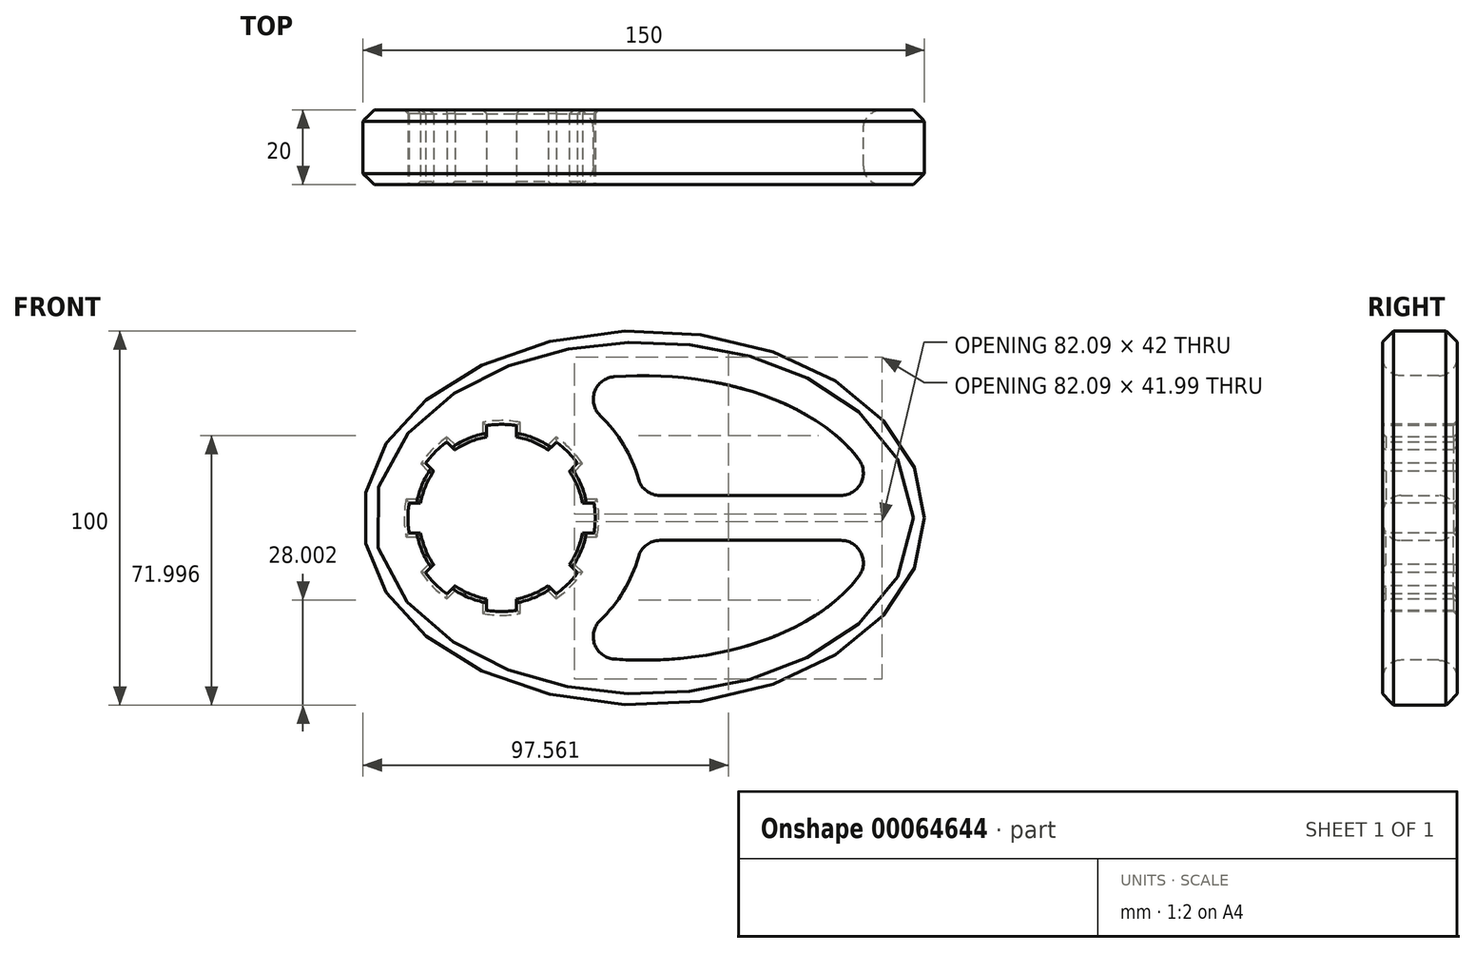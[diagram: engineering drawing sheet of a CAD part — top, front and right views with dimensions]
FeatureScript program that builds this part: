
annotation { "Feature Type Name" : "Feature", "Feature Type Description" : "" }
export const myFeature = defineFeature(function(context is Context, id is Id, definition is map)
    precondition{}
    {
        {
            var Q0;
            Q0=qCreatedBy(makeId("Front.planeOp"),FACE);
            var sketch = newSketch(context, id + "F0", { "sketchPlane" : qUnion([Q0])});
            skEllipse(sketch, "E0", {"center": v(0, 0) * mm, "majorRadius": 75 * mm, "minorRadius": 50 * mm, "majorAxis": v(1, 0)});
            skEllipticalArc(sketch, "E1", {});
            skLineSegment(sketch, "E2", {"start": v(0, 0) * mm, "end": v(-38, 0) * mm});
            skArc(sketch, "E3", {"start": v(-11.66, 27.39) * mm, "mid": v(-5.42, 19.56) * mm, "end": v(-1.44, 10.36) * mm});
            skArc(sketch, "E4", {"start": v(-7.96, 37.7) * mm, "mid": v(-13.15, 33.74) * mm, "end": v(-11.66, 27.39) * mm});
            skArc(sketch, "E5", {"start": v(-1.44, 10.36) * mm, "mid": v(0.71, 7.21) * mm, "end": v(4.33, 6) * mm});
            skArc(sketch, "E6", {"start": v(52.65, 6) * mm, "mid": v(58, 9.3) * mm, "end": v(57.46, 15.59) * mm});
            skLineSegment(sketch, "E7", {"start": v(4.33, 6) * mm, "end": v(52.65, 6) * mm});
            skLineSegment(sketch, "E8.MirrorCS", {"start": v(4.33, -6) * mm, "end": v(52.65, -6) * mm});
            skArc(sketch, "E9.MirrorCS", {"start": v(-1.44, -10.36) * mm, "mid": v(0.71, -7.21) * mm, "end": v(4.33, -6) * mm});
            skArc(sketch, "E10.MirrorCS", {"start": v(-11.66, -27.39) * mm, "mid": v(-5.42, -19.56) * mm, "end": v(-1.44, -10.36) * mm});
            skArc(sketch, "E11.MirrorCS", {"start": v(-7.96, -37.7) * mm, "mid": v(-13.15, -33.74) * mm, "end": v(-11.66, -27.39) * mm});
            skArc(sketch, "E12.MirrorCS", {"start": v(52.65, -6) * mm, "mid": v(58, -9.3) * mm, "end": v(57.46, -15.59) * mm});
            skEllipticalArc(sketch, "E13.trimOffspring", {});
            skCircle(sketch, "E14", {"center": v(-38, 0) * mm, "radius": 22 * mm});
            skPoint(sketch, "E15", {"position": v(75, 0) * mm});
            const initialGuessF0  = {"E1": [0, 0, 1, 0, 0.063, 0.038, 4.5857151122401865, 5.860542602533357], "E1": [0, 0, 1, 0, 0.063, 0.038, 4.5857151122401865, 5.860542602533357], "E13.trimOffspring": [0, 0, 1, 0, 0.063, 0.038, 0.42264270464622916, 1.6974701949393995], "E13.trimOffspring": [0, 0, 1, 0, 0.063, 0.038, 0.42264270464622916, 1.6974701949393995]};
            skSetInitialGuess(sketch, initialGuessF0);
            skSolve(sketch);
        }
        {
            var Q0;
            Q0=makeQuery(id+"F0.imprint","IMPRINT",FACE,{"disambiguationData":[TD([[makeQuery(id+"F0.imprint","IMPRINT",EDGE,{"derivedFrom":sQuery(id+"F0.wireOp",EDGE,"E0")}),1.0]])]});
            extrude(context, id + "F1", {"entities" : qUnion([Q0]), "flatOperationType" : FlatOperationType.REMOVE, "offsetDistance" : 25 * mm, "depth" : 20 * mm, "domain" : OperationDomain.MODEL});
        }
        {
            var Q0;
            Q0=makeQuery(id+"F1.opExtrude","CAP_FACE",FACE,{"disambiguationData":[OSD([sQuery(id+"F0.wireOp",EDGE,"E0"),sQuery(id+"F0.wireOp",EDGE,"E3"),sQuery(id+"F0.wireOp",EDGE,"E4"),sQuery(id+"F0.wireOp",EDGE,"E5"),sQuery(id+"F0.wireOp",EDGE,"E6"),sQuery(id+"F0.wireOp",EDGE,"E7"),sQuery(id+"F0.wireOp",EDGE,"E8.MirrorCS"),sQuery(id+"F0.wireOp",EDGE,"E9.MirrorCS"),sQuery(id+"F0.wireOp",EDGE,"E10.MirrorCS"),sQuery(id+"F0.wireOp",EDGE,"E11.MirrorCS"),sQuery(id+"F0.wireOp",EDGE,"E1"),sQuery(id+"F0.wireOp",EDGE,"E12.MirrorCS"),sQuery(id+"F0.wireOp",EDGE,"E13.trimOffspring"),sQuery(id+"F0.wireOp",EDGE,"E14")])],"isStart":false});
            var sketch = newSketch(context, id + "F2", { "sketchPlane" : qUnion([Q0])});
            skCircle(sketch, "E16", {"center": v(-38, 0) * mm, "radius": 25 * mm});
            skLineSegment(sketch, "E17", {"start": v(-13.32, 4) * mm, "end": v(-16.37, 4) * mm});
            skLineSegment(sketch, "E18", {"start": v(-13.32, -4) * mm, "end": v(-16.37, -4) * mm});
            skSolve(sketch);
        }
        {
            var Q0;
            {var subQ0=sQuery(id+"F2.wireOp",EDGE,"E17");Q0=makeQuery(id+"F2.imprint","IMPRINT",FACE,{"disambiguationData":[TD([[makeQuery(id+"F2.imprint","IMPRINT",EDGE,{"derivedFrom":subQ0}),1.0]])]});}
            extrude(context, id + "F3", {"entities" : qUnion([Q0]), "operationType" : NewBodyOperationType.REMOVE, "endBound" : BoundingType.THROUGH_ALL, "oppositeDirection" : true, "depth" : 25 * mm});
        }
        {
            var Q0;
            Q0=makeQuery(id+"F3.boolean.opBoolean","COPY",FACE,{"derivedFrom":makeQuery(id+"F3.opExtrude","SWEPT_FACE",FACE,{"disambiguationData":[OSD([sQuery(id+"F2.wireOp",EDGE,"E16")])]})});
            var Q1;
            Q1=makeQuery(id+"F3.boolean.opBoolean","COPY",FACE,{"derivedFrom":makeQuery(id+"F3.opExtrude","SWEPT_FACE",FACE,{"disambiguationData":[OSD([sQuery(id+"F2.wireOp",EDGE,"E18")])]})});
            var Q2;
            Q2=makeQuery(id+"F3.boolean.opBoolean","COPY",FACE,{"derivedFrom":makeQuery(id+"F3.opExtrude","SWEPT_FACE",FACE,{"disambiguationData":[OSD([sQuery(id+"F2.wireOp",EDGE,"E17")])]})});
            var Q3;
            Q3=makeQuery(id+"F1.opExtrude","SWEPT_FACE",FACE,{"disambiguationData":[OSD([sQuery(id+"F0.wireOp",EDGE,"E14")])]});
            circularPattern(context, id + "F4", {"operationType" : NewBodyOperationType.REMOVE, "faces" : qUnion([Q0, Q1, Q2]), "axis" : qUnion([Q3]), "angle" : 360 * degree, "instanceCount" : 8, "equalSpace" : true, "patternType" : PatternType.FACE});
        }
        {
            var Q0;
            Q0=makeQuery(id+"F1.opExtrude","CAP_EDGE",EDGE,{"disambiguationData":[OSD([sQuery(id+"F0.wireOp",EDGE,"E0")])],"isStart":false});
            var Q1;
            Q1=makeQuery(id+"F1.opExtrude","CAP_EDGE",EDGE,{"disambiguationData":[OSD([sQuery(id+"F0.wireOp",EDGE,"E0")])],"isStart":true});
            chamfer(context, id + "F5", {"entities" : qUnion([Q0, Q1]), "width" : 3 * mm, "tangentPropagation" : true});
        }
        {
            var Q0;
            Q0=makeQuery(id+"F1.opExtrude","CAP_EDGE",EDGE,{"disambiguationData":[OSD([sQuery(id+"F0.wireOp",EDGE,"E3")])],"isStart":false});
            var Q1;
            Q1=makeQuery(id+"F1.opExtrude","CAP_EDGE",EDGE,{"disambiguationData":[OSD([sQuery(id+"F0.wireOp",EDGE,"E10.MirrorCS")])],"isStart":false});
            var Q2;
            Q2=makeQuery(id+"F1.opExtrude","CAP_EDGE",EDGE,{"disambiguationData":[OSD([sQuery(id+"F0.wireOp",EDGE,"E8.MirrorCS")])],"isStart":true});
            var Q3;
            Q3=makeQuery(id+"F1.opExtrude","CAP_EDGE",EDGE,{"disambiguationData":[OSD([sQuery(id+"F0.wireOp",EDGE,"E7")])],"isStart":true});
            fillet(context, id + "F6", {"entities" : qUnion([Q0, Q1, Q2, Q3]), "radius" : 5 * mm, "tangentPropagation" : true, "allowEdgeOverflow" : false});
        }
        {
            var Q0;
            Q0=makeQuery(id+"F4.opPattern","COPY",EDGE,{"derivedFrom":makeQuery(id+"F3.boolean.opBoolean","COPY",EDGE,{"derivedFrom":makeQuery(id+"F3.opExtrude","CAP_EDGE",EDGE,{"disambiguationData":[OSD([sQuery(id+"F2.wireOp",EDGE,"E16")])],"isStart":true})}),"instanceName":"4"});
            var Q1;
            Q1=makeQuery(id+"F4.opPattern","COPY",EDGE,{"derivedFrom":makeQuery(id+"F3.boolean.opBoolean","COPY",EDGE,{"derivedFrom":makeQuery(id+"F3.opExtrude","CAP_EDGE",EDGE,{"disambiguationData":[OSD([sQuery(id+"F2.wireOp",EDGE,"E17")])],"isStart":true})}),"instanceName":"4"});
            var Q2;
            Q2=makeQuery(id+"F4.opPattern","SPLIT",EDGE,{"disambiguationData":[OD(5.0)],"derivedFrom":makeQuery(id+"F1.opExtrude","CAP_EDGE",EDGE,{"disambiguationData":[OSD([sQuery(id+"F0.wireOp",EDGE,"E14")])],"isStart":false})});
            var Q3;
            Q3=makeQuery(id+"F4.opPattern","COPY",EDGE,{"derivedFrom":makeQuery(id+"F3.boolean.opBoolean","COPY",EDGE,{"derivedFrom":makeQuery(id+"F3.opExtrude","CAP_EDGE",EDGE,{"disambiguationData":[OSD([sQuery(id+"F2.wireOp",EDGE,"E18")])],"isStart":true})}),"instanceName":"5"});
            var Q4;
            Q4=makeQuery(id+"F4.opPattern","COPY",EDGE,{"derivedFrom":makeQuery(id+"F3.boolean.opBoolean","COPY",EDGE,{"derivedFrom":makeQuery(id+"F3.opExtrude","CAP_EDGE",EDGE,{"disambiguationData":[OSD([sQuery(id+"F2.wireOp",EDGE,"E16")])],"isStart":true})}),"instanceName":"5"});
            var Q5;
            Q5=makeQuery(id+"F4.opPattern","COPY",EDGE,{"derivedFrom":makeQuery(id+"F3.boolean.opBoolean","COPY",EDGE,{"derivedFrom":makeQuery(id+"F3.opExtrude","CAP_EDGE",EDGE,{"disambiguationData":[OSD([sQuery(id+"F2.wireOp",EDGE,"E17")])],"isStart":true})}),"instanceName":"5"});
            var Q6;
            Q6=makeQuery(id+"F4.opPattern","SPLIT",EDGE,{"disambiguationData":[OD(6.0)],"derivedFrom":makeQuery(id+"F1.opExtrude","CAP_EDGE",EDGE,{"disambiguationData":[OSD([sQuery(id+"F0.wireOp",EDGE,"E14")])],"isStart":false})});
            var Q7;
            Q7=makeQuery(id+"F4.opPattern","COPY",EDGE,{"derivedFrom":makeQuery(id+"F3.boolean.opBoolean","COPY",EDGE,{"derivedFrom":makeQuery(id+"F3.opExtrude","CAP_EDGE",EDGE,{"disambiguationData":[OSD([sQuery(id+"F2.wireOp",EDGE,"E18")])],"isStart":true})}),"instanceName":"6"});
            var Q8;
            Q8=makeQuery(id+"F4.opPattern","COPY",EDGE,{"derivedFrom":makeQuery(id+"F3.boolean.opBoolean","COPY",EDGE,{"derivedFrom":makeQuery(id+"F3.opExtrude","CAP_EDGE",EDGE,{"disambiguationData":[OSD([sQuery(id+"F2.wireOp",EDGE,"E16")])],"isStart":true})}),"instanceName":"6"});
            var Q9;
            Q9=makeQuery(id+"F4.opPattern","COPY",EDGE,{"derivedFrom":makeQuery(id+"F3.boolean.opBoolean","COPY",EDGE,{"derivedFrom":makeQuery(id+"F3.opExtrude","CAP_EDGE",EDGE,{"disambiguationData":[OSD([sQuery(id+"F2.wireOp",EDGE,"E17")])],"isStart":true})}),"instanceName":"6"});
            var Q10;
            Q10=makeQuery(id+"F4.opPattern","SPLIT",EDGE,{"disambiguationData":[OD(7.0)],"derivedFrom":makeQuery(id+"F1.opExtrude","CAP_EDGE",EDGE,{"disambiguationData":[OSD([sQuery(id+"F0.wireOp",EDGE,"E14")])],"isStart":false})});
            var Q11;
            Q11=makeQuery(id+"F4.opPattern","COPY",EDGE,{"derivedFrom":makeQuery(id+"F3.boolean.opBoolean","COPY",EDGE,{"derivedFrom":makeQuery(id+"F3.opExtrude","CAP_EDGE",EDGE,{"disambiguationData":[OSD([sQuery(id+"F2.wireOp",EDGE,"E18")])],"isStart":true})}),"instanceName":"7"});
            var Q12;
            Q12=makeQuery(id+"F4.opPattern","COPY",EDGE,{"derivedFrom":makeQuery(id+"F3.boolean.opBoolean","COPY",EDGE,{"derivedFrom":makeQuery(id+"F3.opExtrude","CAP_EDGE",EDGE,{"disambiguationData":[OSD([sQuery(id+"F2.wireOp",EDGE,"E16")])],"isStart":true})}),"instanceName":"7"});
            var Q13;
            Q13=makeQuery(id+"F4.opPattern","COPY",EDGE,{"derivedFrom":makeQuery(id+"F3.boolean.opBoolean","COPY",EDGE,{"derivedFrom":makeQuery(id+"F3.opExtrude","CAP_EDGE",EDGE,{"disambiguationData":[OSD([sQuery(id+"F2.wireOp",EDGE,"E17")])],"isStart":true})}),"instanceName":"7"});
            var Q14;
            Q14=makeQuery(id+"F4.opPattern","SPLIT",EDGE,{"disambiguationData":[OD(1.0)],"derivedFrom":makeQuery(id+"F1.opExtrude","CAP_EDGE",EDGE,{"disambiguationData":[OSD([sQuery(id+"F0.wireOp",EDGE,"E14")])],"isStart":false})});
            var Q15;
            Q15=makeQuery(id+"F3.boolean.opBoolean","COPY",EDGE,{"derivedFrom":makeQuery(id+"F3.opExtrude","CAP_EDGE",EDGE,{"disambiguationData":[OSD([sQuery(id+"F2.wireOp",EDGE,"E18")])],"isStart":true})});
            var Q16;
            Q16=makeQuery(id+"F3.boolean.opBoolean","COPY",EDGE,{"derivedFrom":makeQuery(id+"F3.opExtrude","CAP_EDGE",EDGE,{"disambiguationData":[OSD([sQuery(id+"F2.wireOp",EDGE,"E16")])],"isStart":true})});
            var Q17;
            Q17=makeQuery(id+"F3.boolean.opBoolean","COPY",EDGE,{"derivedFrom":makeQuery(id+"F3.opExtrude","CAP_EDGE",EDGE,{"disambiguationData":[OSD([sQuery(id+"F2.wireOp",EDGE,"E17")])],"isStart":true})});
            var Q18;
            Q18=makeQuery(id+"F4.opPattern","SPLIT",EDGE,{"disambiguationData":[OD(0.0)],"derivedFrom":makeQuery(id+"F1.opExtrude","CAP_EDGE",EDGE,{"disambiguationData":[OSD([sQuery(id+"F0.wireOp",EDGE,"E14")])],"isStart":false})});
            var Q19;
            Q19=makeQuery(id+"F4.opPattern","COPY",EDGE,{"derivedFrom":makeQuery(id+"F3.boolean.opBoolean","COPY",EDGE,{"derivedFrom":makeQuery(id+"F3.opExtrude","CAP_EDGE",EDGE,{"disambiguationData":[OSD([sQuery(id+"F2.wireOp",EDGE,"E18")])],"isStart":true})}),"instanceName":"1"});
            var Q20;
            Q20=makeQuery(id+"F4.opPattern","COPY",EDGE,{"derivedFrom":makeQuery(id+"F3.boolean.opBoolean","COPY",EDGE,{"derivedFrom":makeQuery(id+"F3.opExtrude","CAP_EDGE",EDGE,{"disambiguationData":[OSD([sQuery(id+"F2.wireOp",EDGE,"E16")])],"isStart":true})}),"instanceName":"1"});
            var Q21;
            Q21=makeQuery(id+"F4.opPattern","COPY",EDGE,{"derivedFrom":makeQuery(id+"F3.boolean.opBoolean","COPY",EDGE,{"derivedFrom":makeQuery(id+"F3.opExtrude","CAP_EDGE",EDGE,{"disambiguationData":[OSD([sQuery(id+"F2.wireOp",EDGE,"E17")])],"isStart":true})}),"instanceName":"1"});
            var Q22;
            Q22=makeQuery(id+"F4.opPattern","COPY",EDGE,{"derivedFrom":makeQuery(id+"F3.boolean.opBoolean","COPY",EDGE,{"derivedFrom":makeQuery(id+"F3.opExtrude","CAP_EDGE",EDGE,{"disambiguationData":[OSD([sQuery(id+"F2.wireOp",EDGE,"E18")])],"isStart":true})}),"instanceName":"4"});
            var Q23;
            Q23=makeQuery(id+"F4.opPattern","SPLIT",EDGE,{"disambiguationData":[OD(4.0)],"derivedFrom":makeQuery(id+"F1.opExtrude","CAP_EDGE",EDGE,{"disambiguationData":[OSD([sQuery(id+"F0.wireOp",EDGE,"E14")])],"isStart":false})});
            var Q24;
            Q24=makeQuery(id+"F4.opPattern","COPY",EDGE,{"derivedFrom":makeQuery(id+"F3.boolean.opBoolean","COPY",EDGE,{"derivedFrom":makeQuery(id+"F3.opExtrude","CAP_EDGE",EDGE,{"disambiguationData":[OSD([sQuery(id+"F2.wireOp",EDGE,"E17")])],"isStart":true})}),"instanceName":"3"});
            var Q25;
            Q25=makeQuery(id+"F4.opPattern","COPY",EDGE,{"derivedFrom":makeQuery(id+"F3.boolean.opBoolean","COPY",EDGE,{"derivedFrom":makeQuery(id+"F3.opExtrude","CAP_EDGE",EDGE,{"disambiguationData":[OSD([sQuery(id+"F2.wireOp",EDGE,"E16")])],"isStart":true})}),"instanceName":"3"});
            var Q26;
            Q26=makeQuery(id+"F4.opPattern","COPY",EDGE,{"derivedFrom":makeQuery(id+"F3.boolean.opBoolean","COPY",EDGE,{"derivedFrom":makeQuery(id+"F3.opExtrude","CAP_EDGE",EDGE,{"disambiguationData":[OSD([sQuery(id+"F2.wireOp",EDGE,"E18")])],"isStart":true})}),"instanceName":"3"});
            var Q27;
            Q27=makeQuery(id+"F4.opPattern","SPLIT",EDGE,{"disambiguationData":[OD(3.0)],"derivedFrom":makeQuery(id+"F1.opExtrude","CAP_EDGE",EDGE,{"disambiguationData":[OSD([sQuery(id+"F0.wireOp",EDGE,"E14")])],"isStart":false})});
            var Q28;
            Q28=makeQuery(id+"F4.opPattern","COPY",EDGE,{"derivedFrom":makeQuery(id+"F3.boolean.opBoolean","COPY",EDGE,{"derivedFrom":makeQuery(id+"F3.opExtrude","CAP_EDGE",EDGE,{"disambiguationData":[OSD([sQuery(id+"F2.wireOp",EDGE,"E17")])],"isStart":true})}),"instanceName":"2"});
            var Q29;
            Q29=makeQuery(id+"F4.opPattern","COPY",EDGE,{"derivedFrom":makeQuery(id+"F3.boolean.opBoolean","COPY",EDGE,{"derivedFrom":makeQuery(id+"F3.opExtrude","CAP_EDGE",EDGE,{"disambiguationData":[OSD([sQuery(id+"F2.wireOp",EDGE,"E16")])],"isStart":true})}),"instanceName":"2"});
            var Q30;
            Q30=makeQuery(id+"F4.opPattern","COPY",EDGE,{"derivedFrom":makeQuery(id+"F3.boolean.opBoolean","COPY",EDGE,{"derivedFrom":makeQuery(id+"F3.opExtrude","CAP_EDGE",EDGE,{"disambiguationData":[OSD([sQuery(id+"F2.wireOp",EDGE,"E18")])],"isStart":true})}),"instanceName":"2"});
            var Q31;
            Q31=makeQuery(id+"F4.opPattern","SPLIT",EDGE,{"disambiguationData":[OD(2.0)],"derivedFrom":makeQuery(id+"F1.opExtrude","CAP_EDGE",EDGE,{"disambiguationData":[OSD([sQuery(id+"F0.wireOp",EDGE,"E14")])],"isStart":false})});
            chamfer(context, id + "F7", {"entities" : qUnion([Q0, Q1, Q2, Q3, Q4, Q5, Q6, Q7, Q8, Q9, Q10, Q11, Q12, Q13, Q14, Q15, Q16, Q17, Q18, Q19, Q20, Q21, Q22, Q23, Q24, Q25, Q26, Q27, Q28, Q29, Q30, Q31]), "width" : 1 * mm, "tangentPropagation" : true});
        }
        {
            var Q0;
            Q0=makeQuery(id+"F4.opPattern","SPLIT",EDGE,{"disambiguationData":[OD(0.0)],"derivedFrom":makeQuery(id+"F1.opExtrude","CAP_EDGE",EDGE,{"disambiguationData":[OSD([sQuery(id+"F0.wireOp",EDGE,"E14")])],"isStart":true})});
            var Q1;
            Q1=makeQuery(id+"F4.opPattern","COPY",EDGE,{"derivedFrom":makeQuery(id+"F3.boolean.opBoolean","INTERSECT",EDGE,{"derivedFrom":[makeQuery(id+"F1.opExtrude","CAP_FACE",FACE,{"disambiguationData":[OSD([sQuery(id+"F0.wireOp",EDGE,"E0"),sQuery(id+"F0.wireOp",EDGE,"E3"),sQuery(id+"F0.wireOp",EDGE,"E4"),sQuery(id+"F0.wireOp",EDGE,"E5"),sQuery(id+"F0.wireOp",EDGE,"E6"),sQuery(id+"F0.wireOp",EDGE,"E7"),sQuery(id+"F0.wireOp",EDGE,"E8.MirrorCS"),sQuery(id+"F0.wireOp",EDGE,"E9.MirrorCS"),sQuery(id+"F0.wireOp",EDGE,"E10.MirrorCS"),sQuery(id+"F0.wireOp",EDGE,"E11.MirrorCS"),sQuery(id+"F0.wireOp",EDGE,"E1"),sQuery(id+"F0.wireOp",EDGE,"E12.MirrorCS"),sQuery(id+"F0.wireOp",EDGE,"E13.trimOffspring"),sQuery(id+"F0.wireOp",EDGE,"E14")])],"isStart":true}),makeQuery(id+"F3.opExtrude","SWEPT_FACE",FACE,{"disambiguationData":[OSD([sQuery(id+"F2.wireOp",EDGE,"E18")])]})]}),"instanceName":"1"});
            var Q2;
            Q2=makeQuery(id+"F4.opPattern","COPY",EDGE,{"derivedFrom":makeQuery(id+"F3.boolean.opBoolean","INTERSECT",EDGE,{"derivedFrom":[makeQuery(id+"F1.opExtrude","CAP_FACE",FACE,{"disambiguationData":[OSD([sQuery(id+"F0.wireOp",EDGE,"E0"),sQuery(id+"F0.wireOp",EDGE,"E3"),sQuery(id+"F0.wireOp",EDGE,"E4"),sQuery(id+"F0.wireOp",EDGE,"E5"),sQuery(id+"F0.wireOp",EDGE,"E6"),sQuery(id+"F0.wireOp",EDGE,"E7"),sQuery(id+"F0.wireOp",EDGE,"E8.MirrorCS"),sQuery(id+"F0.wireOp",EDGE,"E9.MirrorCS"),sQuery(id+"F0.wireOp",EDGE,"E10.MirrorCS"),sQuery(id+"F0.wireOp",EDGE,"E11.MirrorCS"),sQuery(id+"F0.wireOp",EDGE,"E1"),sQuery(id+"F0.wireOp",EDGE,"E12.MirrorCS"),sQuery(id+"F0.wireOp",EDGE,"E13.trimOffspring"),sQuery(id+"F0.wireOp",EDGE,"E14")])],"isStart":true}),makeQuery(id+"F3.opExtrude","SWEPT_FACE",FACE,{"disambiguationData":[OSD([sQuery(id+"F2.wireOp",EDGE,"E16")])]})]}),"instanceName":"1"});
            var Q3;
            Q3=makeQuery(id+"F4.opPattern","COPY",EDGE,{"derivedFrom":makeQuery(id+"F3.boolean.opBoolean","INTERSECT",EDGE,{"derivedFrom":[makeQuery(id+"F1.opExtrude","CAP_FACE",FACE,{"disambiguationData":[OSD([sQuery(id+"F0.wireOp",EDGE,"E0"),sQuery(id+"F0.wireOp",EDGE,"E3"),sQuery(id+"F0.wireOp",EDGE,"E4"),sQuery(id+"F0.wireOp",EDGE,"E5"),sQuery(id+"F0.wireOp",EDGE,"E6"),sQuery(id+"F0.wireOp",EDGE,"E7"),sQuery(id+"F0.wireOp",EDGE,"E8.MirrorCS"),sQuery(id+"F0.wireOp",EDGE,"E9.MirrorCS"),sQuery(id+"F0.wireOp",EDGE,"E10.MirrorCS"),sQuery(id+"F0.wireOp",EDGE,"E11.MirrorCS"),sQuery(id+"F0.wireOp",EDGE,"E1"),sQuery(id+"F0.wireOp",EDGE,"E12.MirrorCS"),sQuery(id+"F0.wireOp",EDGE,"E13.trimOffspring"),sQuery(id+"F0.wireOp",EDGE,"E14")])],"isStart":true}),makeQuery(id+"F3.opExtrude","SWEPT_FACE",FACE,{"disambiguationData":[OSD([sQuery(id+"F2.wireOp",EDGE,"E17")])]})]}),"instanceName":"1"});
            var Q4;
            Q4=makeQuery(id+"F4.opPattern","SPLIT",EDGE,{"disambiguationData":[OD(2.0)],"derivedFrom":makeQuery(id+"F1.opExtrude","CAP_EDGE",EDGE,{"disambiguationData":[OSD([sQuery(id+"F0.wireOp",EDGE,"E14")])],"isStart":true})});
            var Q5;
            Q5=makeQuery(id+"F4.opPattern","COPY",EDGE,{"derivedFrom":makeQuery(id+"F3.boolean.opBoolean","INTERSECT",EDGE,{"derivedFrom":[makeQuery(id+"F1.opExtrude","CAP_FACE",FACE,{"disambiguationData":[OSD([sQuery(id+"F0.wireOp",EDGE,"E0"),sQuery(id+"F0.wireOp",EDGE,"E3"),sQuery(id+"F0.wireOp",EDGE,"E4"),sQuery(id+"F0.wireOp",EDGE,"E5"),sQuery(id+"F0.wireOp",EDGE,"E6"),sQuery(id+"F0.wireOp",EDGE,"E7"),sQuery(id+"F0.wireOp",EDGE,"E8.MirrorCS"),sQuery(id+"F0.wireOp",EDGE,"E9.MirrorCS"),sQuery(id+"F0.wireOp",EDGE,"E10.MirrorCS"),sQuery(id+"F0.wireOp",EDGE,"E11.MirrorCS"),sQuery(id+"F0.wireOp",EDGE,"E1"),sQuery(id+"F0.wireOp",EDGE,"E12.MirrorCS"),sQuery(id+"F0.wireOp",EDGE,"E13.trimOffspring"),sQuery(id+"F0.wireOp",EDGE,"E14")])],"isStart":true}),makeQuery(id+"F3.opExtrude","SWEPT_FACE",FACE,{"disambiguationData":[OSD([sQuery(id+"F2.wireOp",EDGE,"E17")])]})]}),"instanceName":"1"});
            var Q6;
            Q6=makeQuery(id+"F4.opPattern","COPY",EDGE,{"derivedFrom":makeQuery(id+"F3.boolean.opBoolean","INTERSECT",EDGE,{"derivedFrom":[makeQuery(id+"F1.opExtrude","CAP_FACE",FACE,{"disambiguationData":[OSD([sQuery(id+"F0.wireOp",EDGE,"E0"),sQuery(id+"F0.wireOp",EDGE,"E3"),sQuery(id+"F0.wireOp",EDGE,"E4"),sQuery(id+"F0.wireOp",EDGE,"E5"),sQuery(id+"F0.wireOp",EDGE,"E6"),sQuery(id+"F0.wireOp",EDGE,"E7"),sQuery(id+"F0.wireOp",EDGE,"E8.MirrorCS"),sQuery(id+"F0.wireOp",EDGE,"E9.MirrorCS"),sQuery(id+"F0.wireOp",EDGE,"E10.MirrorCS"),sQuery(id+"F0.wireOp",EDGE,"E11.MirrorCS"),sQuery(id+"F0.wireOp",EDGE,"E1"),sQuery(id+"F0.wireOp",EDGE,"E12.MirrorCS"),sQuery(id+"F0.wireOp",EDGE,"E13.trimOffspring"),sQuery(id+"F0.wireOp",EDGE,"E14")])],"isStart":true}),makeQuery(id+"F3.opExtrude","SWEPT_FACE",FACE,{"disambiguationData":[OSD([sQuery(id+"F2.wireOp",EDGE,"E18")])]})]}),"instanceName":"2"});
            var Q7;
            Q7=makeQuery(id+"F4.opPattern","COPY",EDGE,{"derivedFrom":makeQuery(id+"F3.boolean.opBoolean","INTERSECT",EDGE,{"derivedFrom":[makeQuery(id+"F1.opExtrude","CAP_FACE",FACE,{"disambiguationData":[OSD([sQuery(id+"F0.wireOp",EDGE,"E0"),sQuery(id+"F0.wireOp",EDGE,"E3"),sQuery(id+"F0.wireOp",EDGE,"E4"),sQuery(id+"F0.wireOp",EDGE,"E5"),sQuery(id+"F0.wireOp",EDGE,"E6"),sQuery(id+"F0.wireOp",EDGE,"E7"),sQuery(id+"F0.wireOp",EDGE,"E8.MirrorCS"),sQuery(id+"F0.wireOp",EDGE,"E9.MirrorCS"),sQuery(id+"F0.wireOp",EDGE,"E10.MirrorCS"),sQuery(id+"F0.wireOp",EDGE,"E11.MirrorCS"),sQuery(id+"F0.wireOp",EDGE,"E1"),sQuery(id+"F0.wireOp",EDGE,"E12.MirrorCS"),sQuery(id+"F0.wireOp",EDGE,"E13.trimOffspring"),sQuery(id+"F0.wireOp",EDGE,"E14")])],"isStart":true}),makeQuery(id+"F3.opExtrude","SWEPT_FACE",FACE,{"disambiguationData":[OSD([sQuery(id+"F2.wireOp",EDGE,"E16")])]})]}),"instanceName":"2"});
            var Q8;
            Q8=makeQuery(id+"F4.opPattern","COPY",EDGE,{"derivedFrom":makeQuery(id+"F3.boolean.opBoolean","INTERSECT",EDGE,{"derivedFrom":[makeQuery(id+"F1.opExtrude","CAP_FACE",FACE,{"disambiguationData":[OSD([sQuery(id+"F0.wireOp",EDGE,"E0"),sQuery(id+"F0.wireOp",EDGE,"E3"),sQuery(id+"F0.wireOp",EDGE,"E4"),sQuery(id+"F0.wireOp",EDGE,"E5"),sQuery(id+"F0.wireOp",EDGE,"E6"),sQuery(id+"F0.wireOp",EDGE,"E7"),sQuery(id+"F0.wireOp",EDGE,"E8.MirrorCS"),sQuery(id+"F0.wireOp",EDGE,"E9.MirrorCS"),sQuery(id+"F0.wireOp",EDGE,"E10.MirrorCS"),sQuery(id+"F0.wireOp",EDGE,"E11.MirrorCS"),sQuery(id+"F0.wireOp",EDGE,"E1"),sQuery(id+"F0.wireOp",EDGE,"E12.MirrorCS"),sQuery(id+"F0.wireOp",EDGE,"E13.trimOffspring"),sQuery(id+"F0.wireOp",EDGE,"E14")])],"isStart":true}),makeQuery(id+"F3.opExtrude","SWEPT_FACE",FACE,{"disambiguationData":[OSD([sQuery(id+"F2.wireOp",EDGE,"E17")])]})]}),"instanceName":"2"});
            var Q9;
            Q9=makeQuery(id+"F4.opPattern","SPLIT",EDGE,{"disambiguationData":[OD(3.0)],"derivedFrom":makeQuery(id+"F1.opExtrude","CAP_EDGE",EDGE,{"disambiguationData":[OSD([sQuery(id+"F0.wireOp",EDGE,"E14")])],"isStart":true})});
            var Q10;
            Q10=makeQuery(id+"F4.opPattern","COPY",EDGE,{"derivedFrom":makeQuery(id+"F3.boolean.opBoolean","INTERSECT",EDGE,{"derivedFrom":[makeQuery(id+"F1.opExtrude","CAP_FACE",FACE,{"disambiguationData":[OSD([sQuery(id+"F0.wireOp",EDGE,"E0"),sQuery(id+"F0.wireOp",EDGE,"E3"),sQuery(id+"F0.wireOp",EDGE,"E4"),sQuery(id+"F0.wireOp",EDGE,"E5"),sQuery(id+"F0.wireOp",EDGE,"E6"),sQuery(id+"F0.wireOp",EDGE,"E7"),sQuery(id+"F0.wireOp",EDGE,"E8.MirrorCS"),sQuery(id+"F0.wireOp",EDGE,"E9.MirrorCS"),sQuery(id+"F0.wireOp",EDGE,"E10.MirrorCS"),sQuery(id+"F0.wireOp",EDGE,"E11.MirrorCS"),sQuery(id+"F0.wireOp",EDGE,"E1"),sQuery(id+"F0.wireOp",EDGE,"E12.MirrorCS"),sQuery(id+"F0.wireOp",EDGE,"E13.trimOffspring"),sQuery(id+"F0.wireOp",EDGE,"E14")])],"isStart":true}),makeQuery(id+"F3.opExtrude","SWEPT_FACE",FACE,{"disambiguationData":[OSD([sQuery(id+"F2.wireOp",EDGE,"E18")])]})]}),"instanceName":"3"});
            var Q11;
            Q11=makeQuery(id+"F4.opPattern","COPY",EDGE,{"derivedFrom":makeQuery(id+"F3.boolean.opBoolean","INTERSECT",EDGE,{"derivedFrom":[makeQuery(id+"F1.opExtrude","CAP_FACE",FACE,{"disambiguationData":[OSD([sQuery(id+"F0.wireOp",EDGE,"E0"),sQuery(id+"F0.wireOp",EDGE,"E3"),sQuery(id+"F0.wireOp",EDGE,"E4"),sQuery(id+"F0.wireOp",EDGE,"E5"),sQuery(id+"F0.wireOp",EDGE,"E6"),sQuery(id+"F0.wireOp",EDGE,"E7"),sQuery(id+"F0.wireOp",EDGE,"E8.MirrorCS"),sQuery(id+"F0.wireOp",EDGE,"E9.MirrorCS"),sQuery(id+"F0.wireOp",EDGE,"E10.MirrorCS"),sQuery(id+"F0.wireOp",EDGE,"E11.MirrorCS"),sQuery(id+"F0.wireOp",EDGE,"E1"),sQuery(id+"F0.wireOp",EDGE,"E12.MirrorCS"),sQuery(id+"F0.wireOp",EDGE,"E13.trimOffspring"),sQuery(id+"F0.wireOp",EDGE,"E14")])],"isStart":true}),makeQuery(id+"F3.opExtrude","SWEPT_FACE",FACE,{"disambiguationData":[OSD([sQuery(id+"F2.wireOp",EDGE,"E16")])]})]}),"instanceName":"3"});
            var Q12;
            Q12=makeQuery(id+"F4.opPattern","COPY",EDGE,{"derivedFrom":makeQuery(id+"F3.boolean.opBoolean","INTERSECT",EDGE,{"derivedFrom":[makeQuery(id+"F1.opExtrude","CAP_FACE",FACE,{"disambiguationData":[OSD([sQuery(id+"F0.wireOp",EDGE,"E0"),sQuery(id+"F0.wireOp",EDGE,"E3"),sQuery(id+"F0.wireOp",EDGE,"E4"),sQuery(id+"F0.wireOp",EDGE,"E5"),sQuery(id+"F0.wireOp",EDGE,"E6"),sQuery(id+"F0.wireOp",EDGE,"E7"),sQuery(id+"F0.wireOp",EDGE,"E8.MirrorCS"),sQuery(id+"F0.wireOp",EDGE,"E9.MirrorCS"),sQuery(id+"F0.wireOp",EDGE,"E10.MirrorCS"),sQuery(id+"F0.wireOp",EDGE,"E11.MirrorCS"),sQuery(id+"F0.wireOp",EDGE,"E1"),sQuery(id+"F0.wireOp",EDGE,"E12.MirrorCS"),sQuery(id+"F0.wireOp",EDGE,"E13.trimOffspring"),sQuery(id+"F0.wireOp",EDGE,"E14")])],"isStart":true}),makeQuery(id+"F3.opExtrude","SWEPT_FACE",FACE,{"disambiguationData":[OSD([sQuery(id+"F2.wireOp",EDGE,"E17")])]})]}),"instanceName":"3"});
            var Q13;
            Q13=makeQuery(id+"F4.opPattern","COPY",EDGE,{"derivedFrom":makeQuery(id+"F3.boolean.opBoolean","INTERSECT",EDGE,{"derivedFrom":[makeQuery(id+"F1.opExtrude","CAP_FACE",FACE,{"disambiguationData":[OSD([sQuery(id+"F0.wireOp",EDGE,"E0"),sQuery(id+"F0.wireOp",EDGE,"E3"),sQuery(id+"F0.wireOp",EDGE,"E4"),sQuery(id+"F0.wireOp",EDGE,"E5"),sQuery(id+"F0.wireOp",EDGE,"E6"),sQuery(id+"F0.wireOp",EDGE,"E7"),sQuery(id+"F0.wireOp",EDGE,"E8.MirrorCS"),sQuery(id+"F0.wireOp",EDGE,"E9.MirrorCS"),sQuery(id+"F0.wireOp",EDGE,"E10.MirrorCS"),sQuery(id+"F0.wireOp",EDGE,"E11.MirrorCS"),sQuery(id+"F0.wireOp",EDGE,"E1"),sQuery(id+"F0.wireOp",EDGE,"E12.MirrorCS"),sQuery(id+"F0.wireOp",EDGE,"E13.trimOffspring"),sQuery(id+"F0.wireOp",EDGE,"E14")])],"isStart":true}),makeQuery(id+"F3.opExtrude","SWEPT_FACE",FACE,{"disambiguationData":[OSD([sQuery(id+"F2.wireOp",EDGE,"E18")])]})]}),"instanceName":"4"});
            var Q14;
            Q14=makeQuery(id+"F4.opPattern","COPY",EDGE,{"derivedFrom":makeQuery(id+"F3.boolean.opBoolean","INTERSECT",EDGE,{"derivedFrom":[makeQuery(id+"F1.opExtrude","CAP_FACE",FACE,{"disambiguationData":[OSD([sQuery(id+"F0.wireOp",EDGE,"E0"),sQuery(id+"F0.wireOp",EDGE,"E3"),sQuery(id+"F0.wireOp",EDGE,"E4"),sQuery(id+"F0.wireOp",EDGE,"E5"),sQuery(id+"F0.wireOp",EDGE,"E6"),sQuery(id+"F0.wireOp",EDGE,"E7"),sQuery(id+"F0.wireOp",EDGE,"E8.MirrorCS"),sQuery(id+"F0.wireOp",EDGE,"E9.MirrorCS"),sQuery(id+"F0.wireOp",EDGE,"E10.MirrorCS"),sQuery(id+"F0.wireOp",EDGE,"E11.MirrorCS"),sQuery(id+"F0.wireOp",EDGE,"E1"),sQuery(id+"F0.wireOp",EDGE,"E12.MirrorCS"),sQuery(id+"F0.wireOp",EDGE,"E13.trimOffspring"),sQuery(id+"F0.wireOp",EDGE,"E14")])],"isStart":true}),makeQuery(id+"F3.opExtrude","SWEPT_FACE",FACE,{"disambiguationData":[OSD([sQuery(id+"F2.wireOp",EDGE,"E16")])]})]}),"instanceName":"4"});
            var Q15;
            Q15=makeQuery(id+"F4.opPattern","SPLIT",EDGE,{"disambiguationData":[OD(5.0)],"derivedFrom":makeQuery(id+"F1.opExtrude","CAP_EDGE",EDGE,{"disambiguationData":[OSD([sQuery(id+"F0.wireOp",EDGE,"E14")])],"isStart":true})});
            var Q16;
            Q16=makeQuery(id+"F4.opPattern","COPY",EDGE,{"derivedFrom":makeQuery(id+"F3.boolean.opBoolean","INTERSECT",EDGE,{"derivedFrom":[makeQuery(id+"F1.opExtrude","CAP_FACE",FACE,{"disambiguationData":[OSD([sQuery(id+"F0.wireOp",EDGE,"E0"),sQuery(id+"F0.wireOp",EDGE,"E3"),sQuery(id+"F0.wireOp",EDGE,"E4"),sQuery(id+"F0.wireOp",EDGE,"E5"),sQuery(id+"F0.wireOp",EDGE,"E6"),sQuery(id+"F0.wireOp",EDGE,"E7"),sQuery(id+"F0.wireOp",EDGE,"E8.MirrorCS"),sQuery(id+"F0.wireOp",EDGE,"E9.MirrorCS"),sQuery(id+"F0.wireOp",EDGE,"E10.MirrorCS"),sQuery(id+"F0.wireOp",EDGE,"E11.MirrorCS"),sQuery(id+"F0.wireOp",EDGE,"E1"),sQuery(id+"F0.wireOp",EDGE,"E12.MirrorCS"),sQuery(id+"F0.wireOp",EDGE,"E13.trimOffspring"),sQuery(id+"F0.wireOp",EDGE,"E14")])],"isStart":true}),makeQuery(id+"F3.opExtrude","SWEPT_FACE",FACE,{"disambiguationData":[OSD([sQuery(id+"F2.wireOp",EDGE,"E18")])]})]}),"instanceName":"5"});
            var Q17;
            Q17=makeQuery(id+"F4.opPattern","COPY",EDGE,{"derivedFrom":makeQuery(id+"F3.boolean.opBoolean","INTERSECT",EDGE,{"derivedFrom":[makeQuery(id+"F1.opExtrude","CAP_FACE",FACE,{"disambiguationData":[OSD([sQuery(id+"F0.wireOp",EDGE,"E0"),sQuery(id+"F0.wireOp",EDGE,"E3"),sQuery(id+"F0.wireOp",EDGE,"E4"),sQuery(id+"F0.wireOp",EDGE,"E5"),sQuery(id+"F0.wireOp",EDGE,"E6"),sQuery(id+"F0.wireOp",EDGE,"E7"),sQuery(id+"F0.wireOp",EDGE,"E8.MirrorCS"),sQuery(id+"F0.wireOp",EDGE,"E9.MirrorCS"),sQuery(id+"F0.wireOp",EDGE,"E10.MirrorCS"),sQuery(id+"F0.wireOp",EDGE,"E11.MirrorCS"),sQuery(id+"F0.wireOp",EDGE,"E1"),sQuery(id+"F0.wireOp",EDGE,"E12.MirrorCS"),sQuery(id+"F0.wireOp",EDGE,"E13.trimOffspring"),sQuery(id+"F0.wireOp",EDGE,"E14")])],"isStart":true}),makeQuery(id+"F3.opExtrude","SWEPT_FACE",FACE,{"disambiguationData":[OSD([sQuery(id+"F2.wireOp",EDGE,"E16")])]})]}),"instanceName":"5"});
            var Q18;
            Q18=makeQuery(id+"F4.opPattern","COPY",EDGE,{"derivedFrom":makeQuery(id+"F3.boolean.opBoolean","INTERSECT",EDGE,{"derivedFrom":[makeQuery(id+"F1.opExtrude","CAP_FACE",FACE,{"disambiguationData":[OSD([sQuery(id+"F0.wireOp",EDGE,"E0"),sQuery(id+"F0.wireOp",EDGE,"E3"),sQuery(id+"F0.wireOp",EDGE,"E4"),sQuery(id+"F0.wireOp",EDGE,"E5"),sQuery(id+"F0.wireOp",EDGE,"E6"),sQuery(id+"F0.wireOp",EDGE,"E7"),sQuery(id+"F0.wireOp",EDGE,"E8.MirrorCS"),sQuery(id+"F0.wireOp",EDGE,"E9.MirrorCS"),sQuery(id+"F0.wireOp",EDGE,"E10.MirrorCS"),sQuery(id+"F0.wireOp",EDGE,"E11.MirrorCS"),sQuery(id+"F0.wireOp",EDGE,"E1"),sQuery(id+"F0.wireOp",EDGE,"E12.MirrorCS"),sQuery(id+"F0.wireOp",EDGE,"E13.trimOffspring"),sQuery(id+"F0.wireOp",EDGE,"E14")])],"isStart":true}),makeQuery(id+"F3.opExtrude","SWEPT_FACE",FACE,{"disambiguationData":[OSD([sQuery(id+"F2.wireOp",EDGE,"E17")])]})]}),"instanceName":"5"});
            var Q19;
            Q19=makeQuery(id+"F4.opPattern","SPLIT",EDGE,{"disambiguationData":[OD(6.0)],"derivedFrom":makeQuery(id+"F1.opExtrude","CAP_EDGE",EDGE,{"disambiguationData":[OSD([sQuery(id+"F0.wireOp",EDGE,"E14")])],"isStart":true})});
            var Q20;
            Q20=makeQuery(id+"F4.opPattern","COPY",EDGE,{"derivedFrom":makeQuery(id+"F3.boolean.opBoolean","INTERSECT",EDGE,{"derivedFrom":[makeQuery(id+"F1.opExtrude","CAP_FACE",FACE,{"disambiguationData":[OSD([sQuery(id+"F0.wireOp",EDGE,"E0"),sQuery(id+"F0.wireOp",EDGE,"E3"),sQuery(id+"F0.wireOp",EDGE,"E4"),sQuery(id+"F0.wireOp",EDGE,"E5"),sQuery(id+"F0.wireOp",EDGE,"E6"),sQuery(id+"F0.wireOp",EDGE,"E7"),sQuery(id+"F0.wireOp",EDGE,"E8.MirrorCS"),sQuery(id+"F0.wireOp",EDGE,"E9.MirrorCS"),sQuery(id+"F0.wireOp",EDGE,"E10.MirrorCS"),sQuery(id+"F0.wireOp",EDGE,"E11.MirrorCS"),sQuery(id+"F0.wireOp",EDGE,"E1"),sQuery(id+"F0.wireOp",EDGE,"E12.MirrorCS"),sQuery(id+"F0.wireOp",EDGE,"E13.trimOffspring"),sQuery(id+"F0.wireOp",EDGE,"E14")])],"isStart":true}),makeQuery(id+"F3.opExtrude","SWEPT_FACE",FACE,{"disambiguationData":[OSD([sQuery(id+"F2.wireOp",EDGE,"E18")])]})]}),"instanceName":"6"});
            var Q21;
            Q21=makeQuery(id+"F4.opPattern","COPY",EDGE,{"derivedFrom":makeQuery(id+"F3.boolean.opBoolean","INTERSECT",EDGE,{"derivedFrom":[makeQuery(id+"F1.opExtrude","CAP_FACE",FACE,{"disambiguationData":[OSD([sQuery(id+"F0.wireOp",EDGE,"E0"),sQuery(id+"F0.wireOp",EDGE,"E3"),sQuery(id+"F0.wireOp",EDGE,"E4"),sQuery(id+"F0.wireOp",EDGE,"E5"),sQuery(id+"F0.wireOp",EDGE,"E6"),sQuery(id+"F0.wireOp",EDGE,"E7"),sQuery(id+"F0.wireOp",EDGE,"E8.MirrorCS"),sQuery(id+"F0.wireOp",EDGE,"E9.MirrorCS"),sQuery(id+"F0.wireOp",EDGE,"E10.MirrorCS"),sQuery(id+"F0.wireOp",EDGE,"E11.MirrorCS"),sQuery(id+"F0.wireOp",EDGE,"E1"),sQuery(id+"F0.wireOp",EDGE,"E12.MirrorCS"),sQuery(id+"F0.wireOp",EDGE,"E13.trimOffspring"),sQuery(id+"F0.wireOp",EDGE,"E14")])],"isStart":true}),makeQuery(id+"F3.opExtrude","SWEPT_FACE",FACE,{"disambiguationData":[OSD([sQuery(id+"F2.wireOp",EDGE,"E16")])]})]}),"instanceName":"6"});
            var Q22;
            Q22=makeQuery(id+"F4.opPattern","COPY",EDGE,{"derivedFrom":makeQuery(id+"F3.boolean.opBoolean","INTERSECT",EDGE,{"derivedFrom":[makeQuery(id+"F1.opExtrude","CAP_FACE",FACE,{"disambiguationData":[OSD([sQuery(id+"F0.wireOp",EDGE,"E0"),sQuery(id+"F0.wireOp",EDGE,"E3"),sQuery(id+"F0.wireOp",EDGE,"E4"),sQuery(id+"F0.wireOp",EDGE,"E5"),sQuery(id+"F0.wireOp",EDGE,"E6"),sQuery(id+"F0.wireOp",EDGE,"E7"),sQuery(id+"F0.wireOp",EDGE,"E8.MirrorCS"),sQuery(id+"F0.wireOp",EDGE,"E9.MirrorCS"),sQuery(id+"F0.wireOp",EDGE,"E10.MirrorCS"),sQuery(id+"F0.wireOp",EDGE,"E11.MirrorCS"),sQuery(id+"F0.wireOp",EDGE,"E1"),sQuery(id+"F0.wireOp",EDGE,"E12.MirrorCS"),sQuery(id+"F0.wireOp",EDGE,"E13.trimOffspring"),sQuery(id+"F0.wireOp",EDGE,"E14")])],"isStart":true}),makeQuery(id+"F3.opExtrude","SWEPT_FACE",FACE,{"disambiguationData":[OSD([sQuery(id+"F2.wireOp",EDGE,"E17")])]})]}),"instanceName":"6"});
            var Q23;
            Q23=makeQuery(id+"F4.opPattern","SPLIT",EDGE,{"disambiguationData":[OD(7.0)],"derivedFrom":makeQuery(id+"F1.opExtrude","CAP_EDGE",EDGE,{"disambiguationData":[OSD([sQuery(id+"F0.wireOp",EDGE,"E14")])],"isStart":true})});
            var Q24;
            Q24=makeQuery(id+"F4.opPattern","COPY",EDGE,{"derivedFrom":makeQuery(id+"F3.boolean.opBoolean","INTERSECT",EDGE,{"derivedFrom":[makeQuery(id+"F1.opExtrude","CAP_FACE",FACE,{"disambiguationData":[OSD([sQuery(id+"F0.wireOp",EDGE,"E0"),sQuery(id+"F0.wireOp",EDGE,"E3"),sQuery(id+"F0.wireOp",EDGE,"E4"),sQuery(id+"F0.wireOp",EDGE,"E5"),sQuery(id+"F0.wireOp",EDGE,"E6"),sQuery(id+"F0.wireOp",EDGE,"E7"),sQuery(id+"F0.wireOp",EDGE,"E8.MirrorCS"),sQuery(id+"F0.wireOp",EDGE,"E9.MirrorCS"),sQuery(id+"F0.wireOp",EDGE,"E10.MirrorCS"),sQuery(id+"F0.wireOp",EDGE,"E11.MirrorCS"),sQuery(id+"F0.wireOp",EDGE,"E1"),sQuery(id+"F0.wireOp",EDGE,"E12.MirrorCS"),sQuery(id+"F0.wireOp",EDGE,"E13.trimOffspring"),sQuery(id+"F0.wireOp",EDGE,"E14")])],"isStart":true}),makeQuery(id+"F3.opExtrude","SWEPT_FACE",FACE,{"disambiguationData":[OSD([sQuery(id+"F2.wireOp",EDGE,"E18")])]})]}),"instanceName":"7"});
            var Q25;
            Q25=makeQuery(id+"F4.opPattern","COPY",EDGE,{"derivedFrom":makeQuery(id+"F3.boolean.opBoolean","INTERSECT",EDGE,{"derivedFrom":[makeQuery(id+"F1.opExtrude","CAP_FACE",FACE,{"disambiguationData":[OSD([sQuery(id+"F0.wireOp",EDGE,"E0"),sQuery(id+"F0.wireOp",EDGE,"E3"),sQuery(id+"F0.wireOp",EDGE,"E4"),sQuery(id+"F0.wireOp",EDGE,"E5"),sQuery(id+"F0.wireOp",EDGE,"E6"),sQuery(id+"F0.wireOp",EDGE,"E7"),sQuery(id+"F0.wireOp",EDGE,"E8.MirrorCS"),sQuery(id+"F0.wireOp",EDGE,"E9.MirrorCS"),sQuery(id+"F0.wireOp",EDGE,"E10.MirrorCS"),sQuery(id+"F0.wireOp",EDGE,"E11.MirrorCS"),sQuery(id+"F0.wireOp",EDGE,"E1"),sQuery(id+"F0.wireOp",EDGE,"E12.MirrorCS"),sQuery(id+"F0.wireOp",EDGE,"E13.trimOffspring"),sQuery(id+"F0.wireOp",EDGE,"E14")])],"isStart":true}),makeQuery(id+"F3.opExtrude","SWEPT_FACE",FACE,{"disambiguationData":[OSD([sQuery(id+"F2.wireOp",EDGE,"E16")])]})]}),"instanceName":"7"});
            var Q26;
            Q26=makeQuery(id+"F4.opPattern","SPLIT",EDGE,{"disambiguationData":[OD(1.0)],"derivedFrom":makeQuery(id+"F1.opExtrude","CAP_EDGE",EDGE,{"disambiguationData":[OSD([sQuery(id+"F0.wireOp",EDGE,"E14")])],"isStart":true})});
            var Q27;
            Q27=makeQuery(id+"F4.opPattern","COPY",EDGE,{"derivedFrom":makeQuery(id+"F3.boolean.opBoolean","INTERSECT",EDGE,{"derivedFrom":[makeQuery(id+"F1.opExtrude","CAP_FACE",FACE,{"disambiguationData":[OSD([sQuery(id+"F0.wireOp",EDGE,"E0"),sQuery(id+"F0.wireOp",EDGE,"E3"),sQuery(id+"F0.wireOp",EDGE,"E4"),sQuery(id+"F0.wireOp",EDGE,"E5"),sQuery(id+"F0.wireOp",EDGE,"E6"),sQuery(id+"F0.wireOp",EDGE,"E7"),sQuery(id+"F0.wireOp",EDGE,"E8.MirrorCS"),sQuery(id+"F0.wireOp",EDGE,"E9.MirrorCS"),sQuery(id+"F0.wireOp",EDGE,"E10.MirrorCS"),sQuery(id+"F0.wireOp",EDGE,"E11.MirrorCS"),sQuery(id+"F0.wireOp",EDGE,"E1"),sQuery(id+"F0.wireOp",EDGE,"E12.MirrorCS"),sQuery(id+"F0.wireOp",EDGE,"E13.trimOffspring"),sQuery(id+"F0.wireOp",EDGE,"E14")])],"isStart":true}),makeQuery(id+"F3.opExtrude","SWEPT_FACE",FACE,{"disambiguationData":[OSD([sQuery(id+"F2.wireOp",EDGE,"E17")])]})]}),"instanceName":"7"});
            var Q28;
            Q28=makeQuery(id+"F3.boolean.opBoolean","INTERSECT",EDGE,{"derivedFrom":[makeQuery(id+"F1.opExtrude","CAP_FACE",FACE,{"disambiguationData":[OSD([sQuery(id+"F0.wireOp",EDGE,"E0"),sQuery(id+"F0.wireOp",EDGE,"E3"),sQuery(id+"F0.wireOp",EDGE,"E4"),sQuery(id+"F0.wireOp",EDGE,"E5"),sQuery(id+"F0.wireOp",EDGE,"E6"),sQuery(id+"F0.wireOp",EDGE,"E7"),sQuery(id+"F0.wireOp",EDGE,"E8.MirrorCS"),sQuery(id+"F0.wireOp",EDGE,"E9.MirrorCS"),sQuery(id+"F0.wireOp",EDGE,"E10.MirrorCS"),sQuery(id+"F0.wireOp",EDGE,"E11.MirrorCS"),sQuery(id+"F0.wireOp",EDGE,"E1"),sQuery(id+"F0.wireOp",EDGE,"E12.MirrorCS"),sQuery(id+"F0.wireOp",EDGE,"E13.trimOffspring"),sQuery(id+"F0.wireOp",EDGE,"E14")])],"isStart":true}),makeQuery(id+"F3.opExtrude","SWEPT_FACE",FACE,{"disambiguationData":[OSD([sQuery(id+"F2.wireOp",EDGE,"E18")])]})]});
            var Q29;
            Q29=makeQuery(id+"F3.boolean.opBoolean","INTERSECT",EDGE,{"derivedFrom":[makeQuery(id+"F1.opExtrude","CAP_FACE",FACE,{"disambiguationData":[OSD([sQuery(id+"F0.wireOp",EDGE,"E0"),sQuery(id+"F0.wireOp",EDGE,"E3"),sQuery(id+"F0.wireOp",EDGE,"E4"),sQuery(id+"F0.wireOp",EDGE,"E5"),sQuery(id+"F0.wireOp",EDGE,"E6"),sQuery(id+"F0.wireOp",EDGE,"E7"),sQuery(id+"F0.wireOp",EDGE,"E8.MirrorCS"),sQuery(id+"F0.wireOp",EDGE,"E9.MirrorCS"),sQuery(id+"F0.wireOp",EDGE,"E10.MirrorCS"),sQuery(id+"F0.wireOp",EDGE,"E11.MirrorCS"),sQuery(id+"F0.wireOp",EDGE,"E1"),sQuery(id+"F0.wireOp",EDGE,"E12.MirrorCS"),sQuery(id+"F0.wireOp",EDGE,"E13.trimOffspring"),sQuery(id+"F0.wireOp",EDGE,"E14")])],"isStart":true}),makeQuery(id+"F3.opExtrude","SWEPT_FACE",FACE,{"disambiguationData":[OSD([sQuery(id+"F2.wireOp",EDGE,"E16")])]})]});
            var Q30;
            Q30=makeQuery(id+"F3.boolean.opBoolean","INTERSECT",EDGE,{"derivedFrom":[makeQuery(id+"F1.opExtrude","CAP_FACE",FACE,{"disambiguationData":[OSD([sQuery(id+"F0.wireOp",EDGE,"E0"),sQuery(id+"F0.wireOp",EDGE,"E3"),sQuery(id+"F0.wireOp",EDGE,"E4"),sQuery(id+"F0.wireOp",EDGE,"E5"),sQuery(id+"F0.wireOp",EDGE,"E6"),sQuery(id+"F0.wireOp",EDGE,"E7"),sQuery(id+"F0.wireOp",EDGE,"E8.MirrorCS"),sQuery(id+"F0.wireOp",EDGE,"E9.MirrorCS"),sQuery(id+"F0.wireOp",EDGE,"E10.MirrorCS"),sQuery(id+"F0.wireOp",EDGE,"E11.MirrorCS"),sQuery(id+"F0.wireOp",EDGE,"E1"),sQuery(id+"F0.wireOp",EDGE,"E12.MirrorCS"),sQuery(id+"F0.wireOp",EDGE,"E13.trimOffspring"),sQuery(id+"F0.wireOp",EDGE,"E14")])],"isStart":true}),makeQuery(id+"F3.opExtrude","SWEPT_FACE",FACE,{"disambiguationData":[OSD([sQuery(id+"F2.wireOp",EDGE,"E17")])]})]});
            var Q31;
            Q31=makeQuery(id+"F4.opPattern","SPLIT",EDGE,{"disambiguationData":[OD(4.0)],"derivedFrom":makeQuery(id+"F1.opExtrude","CAP_EDGE",EDGE,{"disambiguationData":[OSD([sQuery(id+"F0.wireOp",EDGE,"E14")])],"isStart":true})});
            var Q32;
            Q32=makeQuery(id+"F4.opPattern","COPY",EDGE,{"derivedFrom":makeQuery(id+"F3.boolean.opBoolean","INTERSECT",EDGE,{"derivedFrom":[makeQuery(id+"F1.opExtrude","CAP_FACE",FACE,{"disambiguationData":[OSD([sQuery(id+"F0.wireOp",EDGE,"E0"),sQuery(id+"F0.wireOp",EDGE,"E3"),sQuery(id+"F0.wireOp",EDGE,"E4"),sQuery(id+"F0.wireOp",EDGE,"E5"),sQuery(id+"F0.wireOp",EDGE,"E6"),sQuery(id+"F0.wireOp",EDGE,"E7"),sQuery(id+"F0.wireOp",EDGE,"E8.MirrorCS"),sQuery(id+"F0.wireOp",EDGE,"E9.MirrorCS"),sQuery(id+"F0.wireOp",EDGE,"E10.MirrorCS"),sQuery(id+"F0.wireOp",EDGE,"E11.MirrorCS"),sQuery(id+"F0.wireOp",EDGE,"E1"),sQuery(id+"F0.wireOp",EDGE,"E12.MirrorCS"),sQuery(id+"F0.wireOp",EDGE,"E13.trimOffspring"),sQuery(id+"F0.wireOp",EDGE,"E14")])],"isStart":true}),makeQuery(id+"F3.opExtrude","SWEPT_FACE",FACE,{"disambiguationData":[OSD([sQuery(id+"F2.wireOp",EDGE,"E17")])]})]}),"instanceName":"4"});
            chamfer(context, id + "F8", {"entities" : qUnion([Q0, Q1, Q2, Q3, Q4, Q5, Q6, Q7, Q8, Q9, Q10, Q11, Q12, Q13, Q14, Q15, Q16, Q17, Q18, Q19, Q20, Q21, Q22, Q23, Q24, Q25, Q26, Q27, Q28, Q29, Q30, Q31, Q32]), "width" : 1 * mm, "tangentPropagation" : true});
        }
    });
